# Revit family: 0067962 Sylvania Lighting Fixture START Waterproof Twin 1500 IP65 EM 7100lm 840
name_source: partatom
category: Lighting Fixtures
revit_build: Autodesk Revit 2016 (Build: 20150220_1215(x64)
units: mm (PartAtom-declared; Revit-internal decimal feet)

## family parameters
Cut with Voids When Loaded = No
Host = Face
Light Source = Yes
OmniClass Number = 23.80.70.11.14
OmniClass Title = General Luminaries, Directional
Part Type = Normal
Room Calculation Point = No
Round Connector Dimension = Use Diameter
Shared = No

## types (2) — shared parameters
AccessoryMaterial = Diffuser-Sylvania-Glow
Apparent Load = 60 VA
Assembly Code = D5020200
AssetType = Fixed
BodyMaterial = Body-Sylvania-Gray
ClassificationName = Uniclass2015
ClassificationValue = EF_70_80
Color Filter = 16777215
Default Elevation = 1219 mm
DiffuserMaterial = Diffuser-Sylvania-Transparent
Dimming Lamp Color Temperature Shift = <None>
DocumentationLiterature = http://www.sylvania-lighting.com
DurationUnit = hours
ElectricShockClassification = Class I
Emit Shape Visible in Rendering = No
Emit from Rectangle Length = 1552 mm  [stored 5.09186 ft]
Emit from Rectangle Width = 90 mm  [stored 0.295276 ft]
ExpectedLife = 50000
IfcExportAs = IfcLightFixtureType
IfcExportType = IfcLightFixtureType
ImpactProtectionIndex = IK08
IngressProtection = IP65
Keynote = 16500
Lamp = LED
LampColourRenderingIndex = 80
LampColourTemperature = 4000 K
LampsType = LED
Length = 1572 mm  [stored 5.15748 ft]
Manufacturer = Feilo Sylvania
ManufacturerName = Feilo Sylvania
Material = polycarbonate housing, polycarbonate diffuser
Model = START Waterproof Twin 1500 IP65 EM 7100lm 840
ModelNumber = 0067962
ModelReference = START Waterproof Twin 1500 IP65 EM 7100lm 840
Name = START Waterproof Twin 1500 IP65 EM 7100lm 840
NominalHeight = 78 mm  [stored 0.255906 ft]
NominalLength = 1578 mm  [stored 5.17717 ft]
PowerConsumption = 60 W
ReflectorMaterial = <By Category>
Tilt Angle = -90.00°
Type Image = <None>
TypeName = START Waterproof Twin 1500 IP65 EM 7100lm 840
URL = http://www.sylvania-lighting.com
Voltage = 0 V
Width = 110 mm  [stored 0.360892 ft]
zero-valued in all types: Cost, NominalWidth, PowerFactor

## per-type parameters (varying)
| type | LampNominalLuminous | LuminousEfficacy | Photometric Web File |
| 0067962 ST WTRPRF T 1500 IP65 EM 7100LM 840 | 7050 lm | 118 lm/W | 0067962.ies |
| 0067962 ST WTRPRF T 1500 IP65 EM 7100LM 840 Emergency mode | 210 lm | 3.504 lm/W | 0067962EM.ies |

note: [stored X ft] marks values corroborated as IEEE doubles in the binary element streams (Revit-internal decimal feet)

## geometry (parser evidence)
native form markers: Sweep x4
no freeform markers — native parametric forms only
